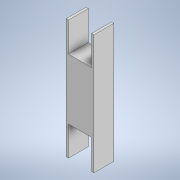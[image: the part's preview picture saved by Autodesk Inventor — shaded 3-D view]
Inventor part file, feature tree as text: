
AUTODESK INVENTOR PART (.ipt)
format: ipt  version: 2020 (Build 240168000, 168)  size: 129,024 bytes
history: native  units: mm
features: extrude x2, sketch x1
ambient origin geometry x8: Origin, YZ Plane, XZ Plane, XY Plane, X Axis, Y Axis, Z Axis, Center Point
bodies: Solid1 (feature_tree)
feature tree (3):
  extrude  "Extrusion1"  Depth=80.0mm
  extrude  "Extrusion2"  Depth=80.0mm
  sketch  "Sketch2"  dims[d0=70.0mm d1=80.0mm d2=80.0mm d3=6.0mm d4=50.0mm d5=0.0mm d7=6.0mm d8=140.0mm d9=0.0mm d10=70.0mm d6=0.5mm]
